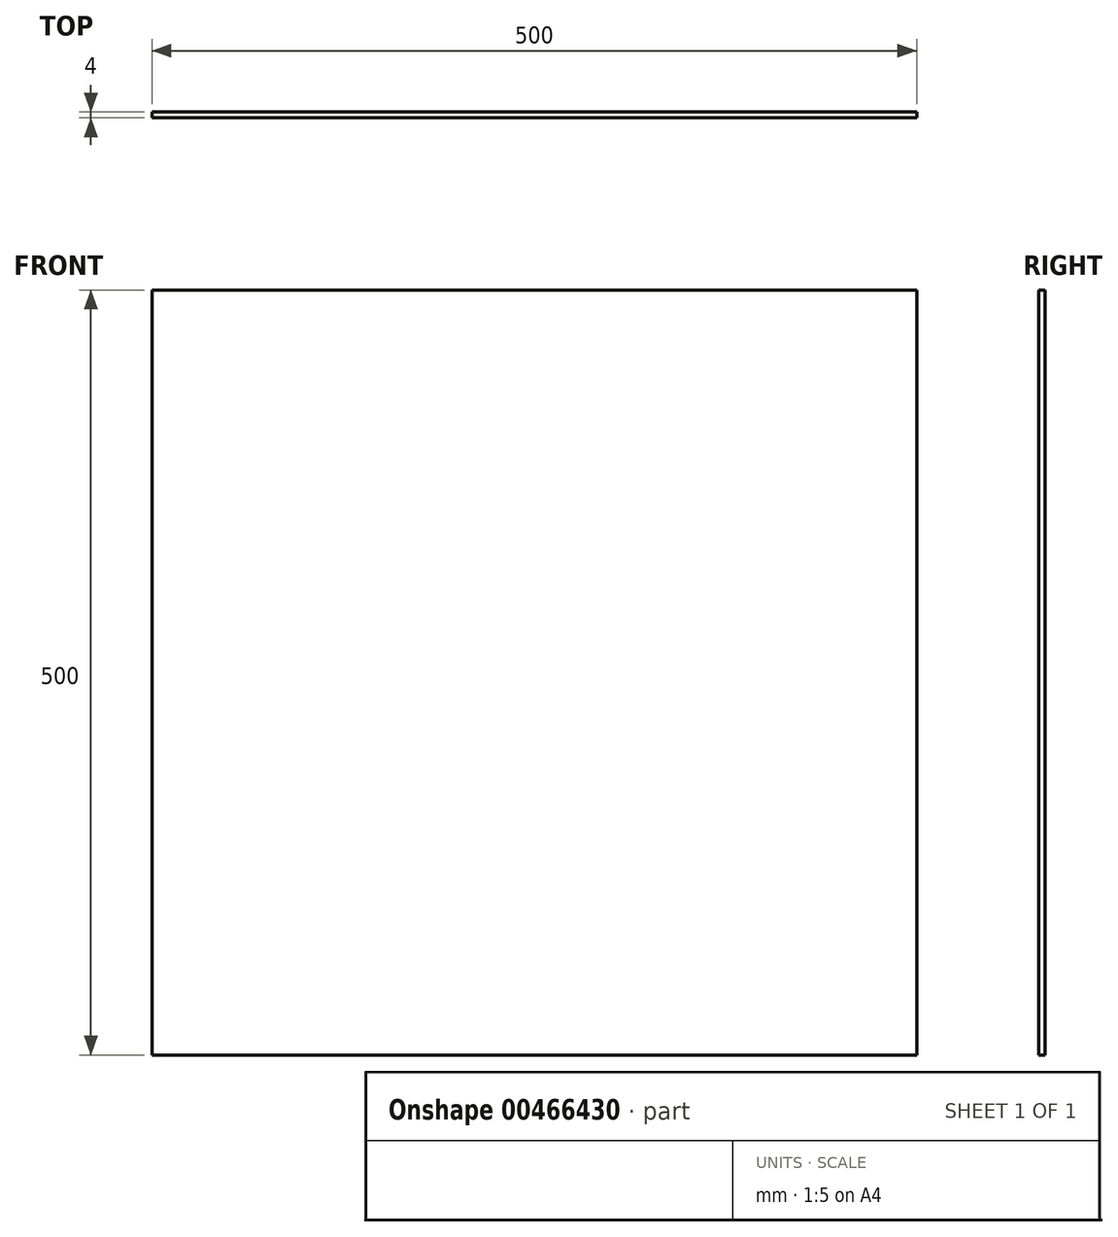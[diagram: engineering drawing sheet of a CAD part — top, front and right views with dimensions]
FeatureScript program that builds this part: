
annotation { "Feature Type Name" : "Feature", "Feature Type Description" : "" }
export const myFeature = defineFeature(function(context is Context, id is Id, definition is map)
    precondition{}
    {
        {
            var Q0;
            Q0=qCreatedBy(makeId("Front.planeOp"),FACE);
            var sketch = newSketch(context, id + "F0", { "sketchPlane" : qUnion([Q0])});
            skLineSegment(sketch, "E0.bottom", {"start": v(250, -250) * mm, "end": v(-250, -250) * mm});
            skLineSegment(sketch, "E0.top", {"start": v(250, 250) * mm, "end": v(-250, 250) * mm});
            skLineSegment(sketch, "E0.left", {"start": v(250, -250) * mm, "end": v(250, 250) * mm});
            skLineSegment(sketch, "E0.right", {"start": v(-250, -250) * mm, "end": v(-250, 250) * mm});
            skPoint(sketch, "E0.middle", {"position": v(0, 0) * mm});
            skSolve(sketch);
        }
        {
            var Q0;
            Q0=makeQuery(id+"F0.imprint","IMPRINT",FACE,{"disambiguationData":[TD([[makeQuery(id+"F0.imprint","IMPRINT",EDGE,{"derivedFrom":sQuery(id+"F0.wireOp",EDGE,"E0.bottom")}),-1.0]])]});
            extrude(context, id + "F1", {"entities" : qUnion([Q0]), "depth" : 4 * mm});
        }
    });
